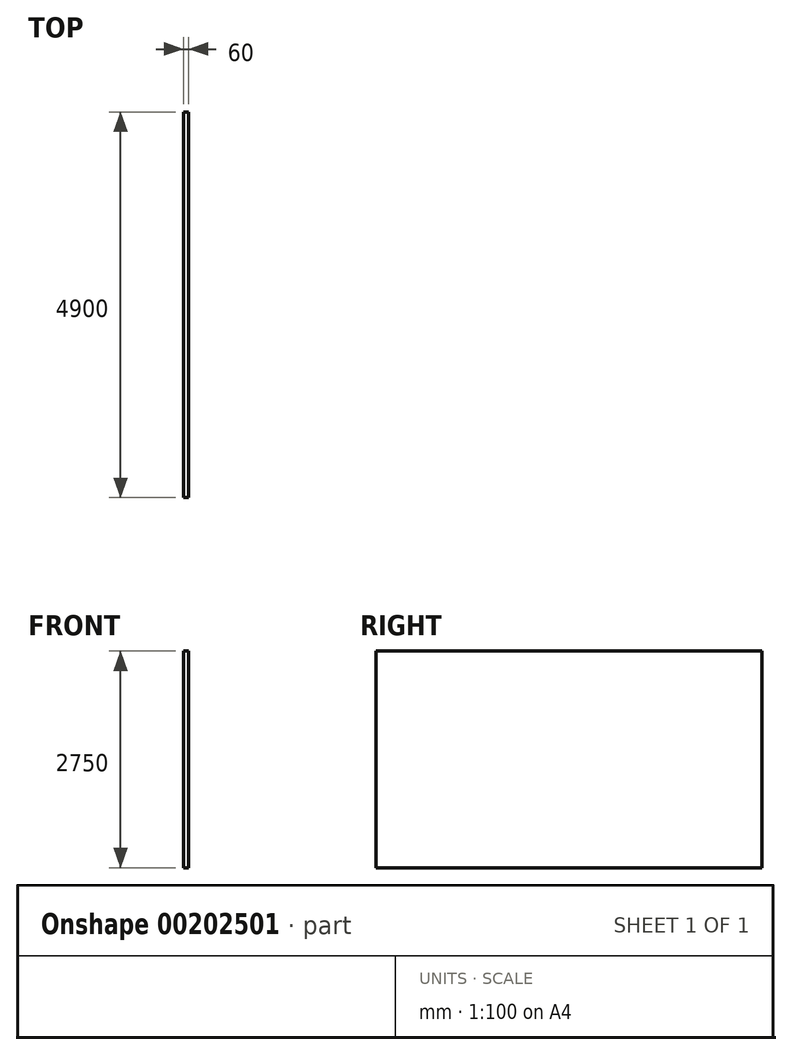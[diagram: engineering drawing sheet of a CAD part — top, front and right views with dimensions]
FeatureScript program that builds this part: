
annotation { "Feature Type Name" : "Feature", "Feature Type Description" : "" }
export const myFeature = defineFeature(function(context is Context, id is Id, definition is map)
    precondition{}
    {
        {
            var Q0;
            Q0=qCreatedBy(makeId("Right.planeOp"),FACE);
            var sketch = newSketch(context, id + "F0", { "sketchPlane" : qUnion([Q0])});
            skLineSegment(sketch, "E0.bottom", {"start": v(-2479.9, 971.69) * mm, "end": v(2420.1, 971.69) * mm});
            skLineSegment(sketch, "E0.top", {"start": v(-2479.9, -1778.31) * mm, "end": v(2420.1, -1778.31) * mm});
            skLineSegment(sketch, "E0.left", {"start": v(-2479.9, 971.69) * mm, "end": v(-2479.9, -1778.31) * mm});
            skLineSegment(sketch, "E0.right", {"start": v(2420.1, 971.69) * mm, "end": v(2420.1, -1778.31) * mm});
            skSolve(sketch);
        }
        {
            var Q0;
            Q0=makeQuery(id+"F0.imprint","IMPRINT",FACE,{"disambiguationData":[TD([[makeQuery(id+"F0.imprint","IMPRINT",EDGE,{"derivedFrom":sQuery(id+"F0.wireOp",EDGE,"E0.bottom")}),-1.0]])]});
            extrude(context, id + "F1", {"entities" : qUnion([Q0]), "depth" : 60 * mm});
        }
    });
